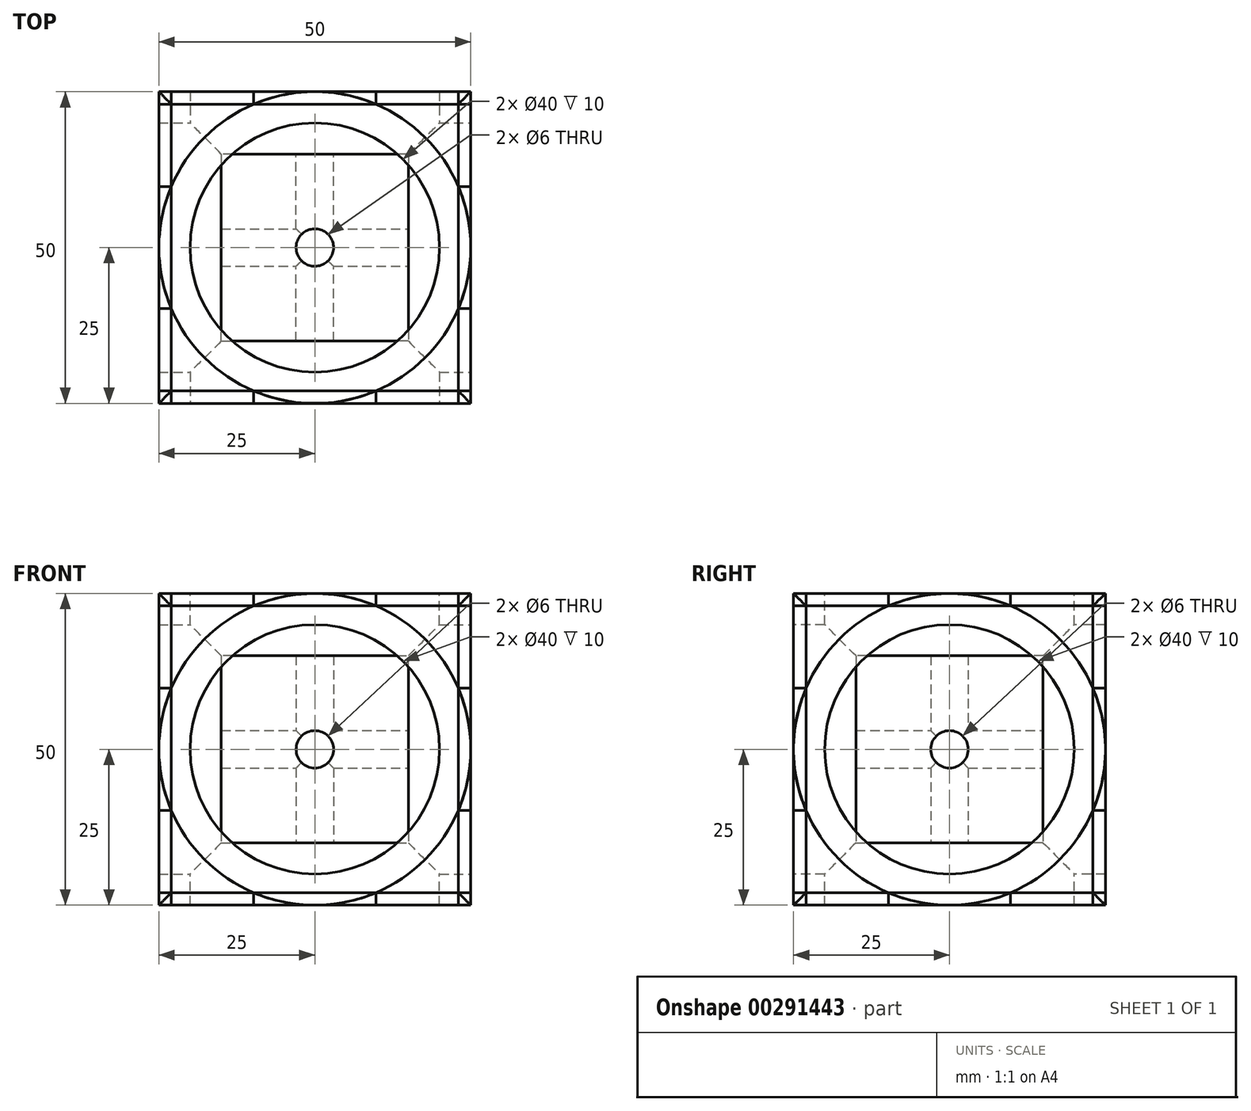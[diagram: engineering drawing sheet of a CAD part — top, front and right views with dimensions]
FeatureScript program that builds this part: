
annotation { "Feature Type Name" : "Feature", "Feature Type Description" : "" }
export const myFeature = defineFeature(function(context is Context, id is Id, definition is map)
    precondition{}
    {
        {
            var Q0;
            Q0=qCreatedBy(makeId("Front.planeOp"),FACE);
            var sketch = newSketch(context, id + "F0", { "sketchPlane" : qUnion([Q0])});
            skLineSegment(sketch, "E0.bottom", {"start": v(-25, 25) * mm, "end": v(25, 25) * mm});
            skLineSegment(sketch, "E0.top", {"start": v(-25, -25) * mm, "end": v(25, -25) * mm});
            skLineSegment(sketch, "E0.left", {"start": v(-25, 25) * mm, "end": v(-25, -25) * mm});
            skLineSegment(sketch, "E0.right", {"start": v(25, 25) * mm, "end": v(25, -25) * mm});
            skSolve(sketch);
        }
        {
            var Q0;
            Q0 = qSketchRegion(id + "F0", true);
            extrude(context, id + "F1", {"entities" : qUnion([Q0]), "depth" : 25 * mm, "hasSecondDirection" : true, "secondDirectionOppositeDirection" : true, "secondDirectionDepth" : 25 * mm});
        }
        {
            var Q0;
            Q0=makeQuery(id+"F1.opExtrude","SWEPT_FACE",FACE,{"disambiguationData":[OSD([sQuery(id+"F0.wireOp",EDGE,"E0.right")])]});
            var sketch = newSketch(context, id + "F2", { "sketchPlane" : qUnion([Q0])});
            skPoint(sketch, "E1", {"position": v(0, 0) * mm});
            skSolve(sketch);
        }
        {
            var Q0;
            Q0=sQuery(id+"F2.wireOp",VERTEX,"E1");
            var Q1;
            Q1=makeQuery(id+"F1.opExtrude","SWEPT_BODY",BODY,{"disambiguationData":[OSD([sQuery(id+"F0.wireOp",EDGE,"E0.bottom"),sQuery(id+"F0.wireOp",EDGE,"E0.top"),sQuery(id+"F0.wireOp",EDGE,"E0.left"),sQuery(id+"F0.wireOp",EDGE,"E0.right")])]});
            hole(context, id + "F3", {"style" : HoleStyle.SIMPLE, "endStyle" : HoleEndStyle.THROUGH, "holeDiameter" : 40 * mm, "tappedDepth" : 12 * mm, "tapClearance" : 3, "locations" : qUnion([Q0]), "scope" : qUnion([Q1])});
        }
        {
            var Q0;
            Q0=makeQuery(id+"F1.opExtrude","SWEPT_FACE",FACE,{"disambiguationData":[OSD([sQuery(id+"F0.wireOp",EDGE,"E0.bottom")])]});
            var sketch = newSketch(context, id + "F4", { "sketchPlane" : qUnion([Q0])});
            skPoint(sketch, "E2", {"position": v(0, 0) * mm});
            skSolve(sketch);
        }
        {
            var Q0;
            Q0=sQuery(id+"F4.wireOp",VERTEX,"E2");
            var Q1;
            Q1=makeQuery(id+"F1.opExtrude","SWEPT_BODY",BODY,{"disambiguationData":[OSD([sQuery(id+"F0.wireOp",EDGE,"E0.bottom"),sQuery(id+"F0.wireOp",EDGE,"E0.top"),sQuery(id+"F0.wireOp",EDGE,"E0.left"),sQuery(id+"F0.wireOp",EDGE,"E0.right")])]});
            hole(context, id + "F5", {"style" : HoleStyle.SIMPLE, "endStyle" : HoleEndStyle.THROUGH, "holeDiameter" : 40 * mm, "tappedDepth" : 12 * mm, "tapClearance" : 3, "locations" : qUnion([Q0]), "scope" : qUnion([Q1])});
        }
        {
            var Q0;
            Q0=makeQuery(id+"F1.opExtrude","CAP_FACE",FACE,{"disambiguationData":[OSD([sQuery(id+"F0.wireOp",EDGE,"E0.bottom"),sQuery(id+"F0.wireOp",EDGE,"E0.top"),sQuery(id+"F0.wireOp",EDGE,"E0.left"),sQuery(id+"F0.wireOp",EDGE,"E0.right")])],"isStart":false});
            var sketch = newSketch(context, id + "F6", { "sketchPlane" : qUnion([Q0])});
            skPoint(sketch, "E3", {"position": v(0, 0) * mm});
            skSolve(sketch);
        }
        {
            var Q0;
            Q0=sQuery(id+"F6.wireOp",VERTEX,"E3");
            var Q1;
            Q1=makeQuery(id+"F1.opExtrude","SWEPT_BODY",BODY,{"disambiguationData":[OSD([sQuery(id+"F0.wireOp",EDGE,"E0.bottom"),sQuery(id+"F0.wireOp",EDGE,"E0.top"),sQuery(id+"F0.wireOp",EDGE,"E0.left"),sQuery(id+"F0.wireOp",EDGE,"E0.right")])]});
            hole(context, id + "F7", {"style" : HoleStyle.SIMPLE, "endStyle" : HoleEndStyle.THROUGH, "holeDiameter" : 40 * mm, "tappedDepth" : 12 * mm, "tapClearance" : 3, "locations" : qUnion([Q0]), "scope" : qUnion([Q1])});
        }
        {
            var Q0;
            Q0=qCreatedBy(makeId("Top.planeOp"),FACE);
            var sketch = newSketch(context, id + "F8", { "sketchPlane" : qUnion([Q0])});
            skLineSegment(sketch, "E4.bottom", {"start": v(-15, 15) * mm, "end": v(15, 15) * mm});
            skLineSegment(sketch, "E4.top", {"start": v(-15, -15) * mm, "end": v(15, -15) * mm});
            skLineSegment(sketch, "E4.left", {"start": v(-15, 15) * mm, "end": v(-15, -15) * mm});
            skLineSegment(sketch, "E4.right", {"start": v(15, 15) * mm, "end": v(15, -15) * mm});
            skSolve(sketch);
        }
        {
            var Q0;
            Q0=makeQuery(id+"F8.imprint","IMPRINT",FACE,{"disambiguationData":[TD([[makeQuery(id+"F8.imprint","IMPRINT",EDGE,{"derivedFrom":sQuery(id+"F8.wireOp",EDGE,"E4.bottom")}),-1.0]])]});
            extrude(context, id + "F9", {"entities" : qUnion([Q0]), "operationType" : NewBodyOperationType.ADD, "depth" : 15 * mm, "hasSecondDirection" : true, "secondDirectionOppositeDirection" : true, "secondDirectionDepth" : 15 * mm});
        }
        {
            var Q0;
            Q0=makeQuery(id+"F1.opExtrude","CAP_FACE",FACE,{"disambiguationData":[OSD([sQuery(id+"F0.wireOp",EDGE,"E0.bottom"),sQuery(id+"F0.wireOp",EDGE,"E0.top"),sQuery(id+"F0.wireOp",EDGE,"E0.left"),sQuery(id+"F0.wireOp",EDGE,"E0.right")])],"isStart":true});
            var sketch = newSketch(context, id + "F10", { "sketchPlane" : qUnion([Q0])});
            skCircle(sketch, "E5", {"center": v(0, 0) * mm, "radius": 25 * mm});
            skLineSegment(sketch, "E6.bottom", {"start": v(25, -25) * mm, "end": v(-25, -25) * mm});
            skLineSegment(sketch, "E6.top", {"start": v(25, 25) * mm, "end": v(-25, 25) * mm});
            skLineSegment(sketch, "E6.left", {"start": v(25, -25) * mm, "end": v(25, 25) * mm});
            skLineSegment(sketch, "E6.right", {"start": v(-25, -25) * mm, "end": v(-25, 25) * mm});
            skSolve(sketch);
        }
        {
            var Q0;
            Q0=makeQuery(id+"F1.opExtrude","SWEPT_FACE",FACE,{"disambiguationData":[OSD([sQuery(id+"F0.wireOp",EDGE,"E0.left")])]});
            var sketch = newSketch(context, id + "F11", { "sketchPlane" : qUnion([Q0])});
            skCircle(sketch, "E7", {"center": v(0, 0) * mm, "radius": 25 * mm});
            skLineSegment(sketch, "E8.bottom", {"start": v(25, -25) * mm, "end": v(-25, -25) * mm});
            skLineSegment(sketch, "E8.top", {"start": v(25, 25) * mm, "end": v(-25, 25) * mm});
            skLineSegment(sketch, "E8.left", {"start": v(25, -25) * mm, "end": v(25, 25) * mm});
            skLineSegment(sketch, "E8.right", {"start": v(-25, -25) * mm, "end": v(-25, 25) * mm});
            skSolve(sketch);
        }
        {
            var Q0;
            Q0=makeQuery(id+"F1.opExtrude","SWEPT_FACE",FACE,{"disambiguationData":[OSD([sQuery(id+"F0.wireOp",EDGE,"E0.bottom")])]});
            var sketch = newSketch(context, id + "F12", { "sketchPlane" : qUnion([Q0])});
            skCircle(sketch, "E9", {"center": v(0, 0) * mm, "radius": 25 * mm});
            skLineSegment(sketch, "E10.bottom", {"start": v(25, -25) * mm, "end": v(-25, -25) * mm});
            skLineSegment(sketch, "E10.top", {"start": v(25, 25) * mm, "end": v(-25, 25) * mm});
            skLineSegment(sketch, "E10.left", {"start": v(25, -25) * mm, "end": v(25, 25) * mm});
            skLineSegment(sketch, "E10.right", {"start": v(-25, -25) * mm, "end": v(-25, 25) * mm});
            skSolve(sketch);
        }
        {
            var Q0;
            Q0=makeQuery(id+"F1.opExtrude","SWEPT_FACE",FACE,{"disambiguationData":[OSD([sQuery(id+"F0.wireOp",EDGE,"E0.right")])]});
            var sketch = newSketch(context, id + "F13", { "sketchPlane" : qUnion([Q0])});
            skCircle(sketch, "E11", {"center": v(0, 0) * mm, "radius": 25 * mm});
            skLineSegment(sketch, "E12.bottom", {"start": v(25, -25) * mm, "end": v(-25, -25) * mm});
            skLineSegment(sketch, "E12.top", {"start": v(25, 25) * mm, "end": v(-25, 25) * mm});
            skLineSegment(sketch, "E12.left", {"start": v(25, -25) * mm, "end": v(25, 25) * mm});
            skLineSegment(sketch, "E12.right", {"start": v(-25, -25) * mm, "end": v(-25, 25) * mm});
            skSolve(sketch);
        }
        {
            var Q0;
            Q0=makeQuery(id+"F1.opExtrude","SWEPT_FACE",FACE,{"disambiguationData":[OSD([sQuery(id+"F0.wireOp",EDGE,"E0.top")])]});
            var sketch = newSketch(context, id + "F14", { "sketchPlane" : qUnion([Q0])});
            skCircle(sketch, "E13", {"center": v(0, 0) * mm, "radius": 25 * mm});
            skLineSegment(sketch, "E14.bottom", {"start": v(25, -25) * mm, "end": v(-25, -25) * mm});
            skLineSegment(sketch, "E14.top", {"start": v(25, 25) * mm, "end": v(-25, 25) * mm});
            skLineSegment(sketch, "E14.left", {"start": v(25, -25) * mm, "end": v(25, 25) * mm});
            skLineSegment(sketch, "E14.right", {"start": v(-25, -25) * mm, "end": v(-25, 25) * mm});
            skSolve(sketch);
        }
        {
            var Q0;
            Q0=makeQuery(id+"F1.opExtrude","CAP_FACE",FACE,{"disambiguationData":[OSD([sQuery(id+"F0.wireOp",EDGE,"E0.bottom"),sQuery(id+"F0.wireOp",EDGE,"E0.top"),sQuery(id+"F0.wireOp",EDGE,"E0.left"),sQuery(id+"F0.wireOp",EDGE,"E0.right")])],"isStart":false});
            var sketch = newSketch(context, id + "F15", { "sketchPlane" : qUnion([Q0])});
            skCircle(sketch, "E15", {"center": v(0, 0) * mm, "radius": 25 * mm});
            skLineSegment(sketch, "E16.bottom", {"start": v(25, -25) * mm, "end": v(-25, -25) * mm});
            skLineSegment(sketch, "E16.top", {"start": v(25, 25) * mm, "end": v(-25, 25) * mm});
            skLineSegment(sketch, "E16.left", {"start": v(25, -25) * mm, "end": v(25, 25) * mm});
            skLineSegment(sketch, "E16.right", {"start": v(-25, -25) * mm, "end": v(-25, 25) * mm});
            skSolve(sketch);
        }
        {
            var Q0;
            Q0=makeQuery(id+"F1.opExtrude","CAP_FACE",FACE,{"disambiguationData":[OSD([sQuery(id+"F0.wireOp",EDGE,"E0.bottom"),sQuery(id+"F0.wireOp",EDGE,"E0.top"),sQuery(id+"F0.wireOp",EDGE,"E0.left"),sQuery(id+"F0.wireOp",EDGE,"E0.right")])],"isStart":true});
            var sketch = newSketch(context, id + "F16", { "sketchPlane" : qUnion([Q0])});
            skCircle(sketch, "E17", {"center": v(0, 0) * mm, "radius": 25 * mm});
            skLineSegment(sketch, "E18.bottom", {"start": v(25, -25) * mm, "end": v(-25, -25) * mm});
            skLineSegment(sketch, "E18.top", {"start": v(25, 25) * mm, "end": v(-25, 25) * mm});
            skLineSegment(sketch, "E18.left", {"start": v(25, -25) * mm, "end": v(25, 25) * mm});
            skLineSegment(sketch, "E18.right", {"start": v(-25, -25) * mm, "end": v(-25, 25) * mm});
            skSolve(sketch);
        }
        {
            var Q0;
            {var subQ0=sQuery(id+"F10.wireOp",EDGE,"E6.top");var subQ1=sQuery(id+"F10.wireOp",EDGE,"E5");var subQ2=makeQuery(id+"F10.imprint","INTERSECT",VERTEX,{"derivedFrom":[subQ1,subQ0]});Q0=makeQuery(id+"F10.imprint","IMPRINT",FACE,{"disambiguationData":[TD([[makeQuery(id+"F10.imprint","IMPRINT",EDGE,{"disambiguationData":[TD([[subQ2,1.0]])],"derivedFrom":subQ1}),-1.0]])]});}
            var Q1;
            {var subQ0=sQuery(id+"F10.wireOp",EDGE,"E6.top");var subQ1=sQuery(id+"F10.wireOp",EDGE,"E5");var subQ2=makeQuery(id+"F10.imprint","INTERSECT",VERTEX,{"derivedFrom":[subQ1,subQ0]});Q1=makeQuery(id+"F10.imprint","IMPRINT",FACE,{"disambiguationData":[TD([[makeQuery(id+"F10.imprint","IMPRINT",EDGE,{"disambiguationData":[TD([[subQ2,-1.0]])],"derivedFrom":subQ1}),-1.0]])]});}
            var Q2;
            {var subQ0=sQuery(id+"F10.wireOp",EDGE,"E6.right");var subQ1=sQuery(id+"F10.wireOp",EDGE,"E5");var subQ2=makeQuery(id+"F10.imprint","INTERSECT",VERTEX,{"derivedFrom":[subQ1,subQ0]});Q2=makeQuery(id+"F10.imprint","IMPRINT",FACE,{"disambiguationData":[TD([[makeQuery(id+"F10.imprint","IMPRINT",EDGE,{"disambiguationData":[TD([[subQ2,-1.0]])],"derivedFrom":subQ1}),-1.0]])]});}
            var Q3;
            {var subQ0=sQuery(id+"F10.wireOp",EDGE,"E6.left");var subQ1=sQuery(id+"F10.wireOp",EDGE,"E5");var subQ2=makeQuery(id+"F10.imprint","INTERSECT",VERTEX,{"derivedFrom":[subQ1,subQ0]});Q3=makeQuery(id+"F10.imprint","IMPRINT",FACE,{"disambiguationData":[TD([[makeQuery(id+"F10.imprint","IMPRINT",EDGE,{"disambiguationData":[TD([[subQ2,1.0]])],"derivedFrom":subQ1}),-1.0]])]});}
            extrude(context, id + "F17", {"entities" : qUnion([Q0, Q1, Q2, Q3]), "operationType" : NewBodyOperationType.REMOVE, "depth" : 2 * mm});
        }
        {
            var Q0;
            {var subQ0=sQuery(id+"F15.wireOp",EDGE,"E16.top");var subQ1=sQuery(id+"F15.wireOp",EDGE,"E15");var subQ2=makeQuery(id+"F15.imprint","INTERSECT",VERTEX,{"derivedFrom":[subQ1,subQ0]});Q0=makeQuery(id+"F15.imprint","IMPRINT",FACE,{"disambiguationData":[TD([[makeQuery(id+"F15.imprint","IMPRINT",EDGE,{"disambiguationData":[TD([[subQ2,-1.0]])],"derivedFrom":subQ1}),-1.0]])]});}
            var Q1;
            {var subQ0=sQuery(id+"F15.wireOp",EDGE,"E16.right");var subQ1=sQuery(id+"F15.wireOp",EDGE,"E15");var subQ2=makeQuery(id+"F15.imprint","INTERSECT",VERTEX,{"derivedFrom":[subQ1,subQ0]});Q1=makeQuery(id+"F15.imprint","IMPRINT",FACE,{"disambiguationData":[TD([[makeQuery(id+"F15.imprint","IMPRINT",EDGE,{"disambiguationData":[TD([[subQ2,-1.0]])],"derivedFrom":subQ1}),-1.0]])]});}
            var Q2;
            {var subQ0=sQuery(id+"F15.wireOp",EDGE,"E16.left");var subQ1=sQuery(id+"F15.wireOp",EDGE,"E15");var subQ2=makeQuery(id+"F15.imprint","INTERSECT",VERTEX,{"derivedFrom":[subQ1,subQ0]});Q2=makeQuery(id+"F15.imprint","IMPRINT",FACE,{"disambiguationData":[TD([[makeQuery(id+"F15.imprint","IMPRINT",EDGE,{"disambiguationData":[TD([[subQ2,1.0]])],"derivedFrom":subQ1}),-1.0]])]});}
            var Q3;
            {var subQ0=sQuery(id+"F15.wireOp",EDGE,"E16.top");var subQ1=sQuery(id+"F15.wireOp",EDGE,"E15");var subQ2=makeQuery(id+"F15.imprint","INTERSECT",VERTEX,{"derivedFrom":[subQ1,subQ0]});Q3=makeQuery(id+"F15.imprint","IMPRINT",FACE,{"disambiguationData":[TD([[makeQuery(id+"F15.imprint","IMPRINT",EDGE,{"disambiguationData":[TD([[subQ2,1.0]])],"derivedFrom":subQ1}),-1.0]])]});}
            extrude(context, id + "F18", {"entities" : qUnion([Q0, Q1, Q2, Q3]), "operationType" : NewBodyOperationType.REMOVE, "oppositeDirection" : true, "depth" : 2 * mm});
        }
        {
            var Q0;
            {var subQ0=sQuery(id+"F12.wireOp",EDGE,"E10.right");var subQ1=sQuery(id+"F12.wireOp",EDGE,"E9");var subQ2=makeQuery(id+"F12.imprint","INTERSECT",VERTEX,{"derivedFrom":[subQ1,subQ0]});Q0=makeQuery(id+"F12.imprint","IMPRINT",FACE,{"disambiguationData":[TD([[makeQuery(id+"F12.imprint","IMPRINT",EDGE,{"disambiguationData":[TD([[subQ2,-1.0]])],"derivedFrom":subQ1}),-1.0]])]});}
            var Q1;
            {var subQ0=sQuery(id+"F12.wireOp",EDGE,"E10.top");var subQ1=sQuery(id+"F12.wireOp",EDGE,"E9");var subQ2=makeQuery(id+"F12.imprint","INTERSECT",VERTEX,{"derivedFrom":[subQ1,subQ0]});Q1=makeQuery(id+"F12.imprint","IMPRINT",FACE,{"disambiguationData":[TD([[makeQuery(id+"F12.imprint","IMPRINT",EDGE,{"disambiguationData":[TD([[subQ2,-1.0]])],"derivedFrom":subQ1}),-1.0]])]});}
            var Q2;
            {var subQ0=sQuery(id+"F12.wireOp",EDGE,"E10.top");var subQ1=sQuery(id+"F12.wireOp",EDGE,"E9");var subQ2=makeQuery(id+"F12.imprint","INTERSECT",VERTEX,{"derivedFrom":[subQ1,subQ0]});Q2=makeQuery(id+"F12.imprint","IMPRINT",FACE,{"disambiguationData":[TD([[makeQuery(id+"F12.imprint","IMPRINT",EDGE,{"disambiguationData":[TD([[subQ2,1.0]])],"derivedFrom":subQ1}),-1.0]])]});}
            var Q3;
            {var subQ0=sQuery(id+"F12.wireOp",EDGE,"E10.left");var subQ1=sQuery(id+"F12.wireOp",EDGE,"E9");var subQ2=makeQuery(id+"F12.imprint","INTERSECT",VERTEX,{"derivedFrom":[subQ1,subQ0]});Q3=makeQuery(id+"F12.imprint","IMPRINT",FACE,{"disambiguationData":[TD([[makeQuery(id+"F12.imprint","IMPRINT",EDGE,{"disambiguationData":[TD([[subQ2,1.0]])],"derivedFrom":subQ1}),-1.0]])]});}
            extrude(context, id + "F19", {"entities" : qUnion([Q0, Q1, Q2, Q3]), "operationType" : NewBodyOperationType.REMOVE, "oppositeDirection" : true, "depth" : 2 * mm});
        }
        {
            var Q0;
            {var subQ0=sQuery(id+"F13.wireOp",EDGE,"E12.top");var subQ1=sQuery(id+"F13.wireOp",EDGE,"E11");var subQ2=makeQuery(id+"F13.imprint","INTERSECT",VERTEX,{"derivedFrom":[subQ1,subQ0]});Q0=makeQuery(id+"F13.imprint","IMPRINT",FACE,{"disambiguationData":[TD([[makeQuery(id+"F13.imprint","IMPRINT",EDGE,{"disambiguationData":[TD([[subQ2,-1.0]])],"derivedFrom":subQ1}),-1.0]])]});}
            var Q1;
            {var subQ0=sQuery(id+"F13.wireOp",EDGE,"E12.top");var subQ1=sQuery(id+"F13.wireOp",EDGE,"E11");var subQ2=makeQuery(id+"F13.imprint","INTERSECT",VERTEX,{"derivedFrom":[subQ1,subQ0]});Q1=makeQuery(id+"F13.imprint","IMPRINT",FACE,{"disambiguationData":[TD([[makeQuery(id+"F13.imprint","IMPRINT",EDGE,{"disambiguationData":[TD([[subQ2,1.0]])],"derivedFrom":subQ1}),-1.0]])]});}
            var Q2;
            {var subQ0=sQuery(id+"F13.wireOp",EDGE,"E12.left");var subQ1=sQuery(id+"F13.wireOp",EDGE,"E11");var subQ2=makeQuery(id+"F13.imprint","INTERSECT",VERTEX,{"derivedFrom":[subQ1,subQ0]});Q2=makeQuery(id+"F13.imprint","IMPRINT",FACE,{"disambiguationData":[TD([[makeQuery(id+"F13.imprint","IMPRINT",EDGE,{"disambiguationData":[TD([[subQ2,1.0]])],"derivedFrom":subQ1}),-1.0]])]});}
            var Q3;
            {var subQ0=sQuery(id+"F13.wireOp",EDGE,"E12.right");var subQ1=sQuery(id+"F13.wireOp",EDGE,"E11");var subQ2=makeQuery(id+"F13.imprint","INTERSECT",VERTEX,{"derivedFrom":[subQ1,subQ0]});Q3=makeQuery(id+"F13.imprint","IMPRINT",FACE,{"disambiguationData":[TD([[makeQuery(id+"F13.imprint","IMPRINT",EDGE,{"disambiguationData":[TD([[subQ2,-1.0]])],"derivedFrom":subQ1}),-1.0]])]});}
            extrude(context, id + "F20", {"entities" : qUnion([Q0, Q1, Q2, Q3]), "operationType" : NewBodyOperationType.REMOVE, "oppositeDirection" : true, "depth" : 2 * mm});
        }
        {
            var Q0;
            {var subQ0=sQuery(id+"F16.wireOp",EDGE,"E18.top");var subQ1=sQuery(id+"F16.wireOp",EDGE,"E17");var subQ2=makeQuery(id+"F16.imprint","INTERSECT",VERTEX,{"derivedFrom":[subQ1,subQ0]});Q0=makeQuery(id+"F16.imprint","IMPRINT",FACE,{"disambiguationData":[TD([[makeQuery(id+"F16.imprint","IMPRINT",EDGE,{"disambiguationData":[TD([[subQ2,-1.0]])],"derivedFrom":subQ1}),-1.0]])]});}
            var Q1;
            {var subQ0=sQuery(id+"F16.wireOp",EDGE,"E18.top");var subQ1=sQuery(id+"F16.wireOp",EDGE,"E17");var subQ2=makeQuery(id+"F16.imprint","INTERSECT",VERTEX,{"derivedFrom":[subQ1,subQ0]});Q1=makeQuery(id+"F16.imprint","IMPRINT",FACE,{"disambiguationData":[TD([[makeQuery(id+"F16.imprint","IMPRINT",EDGE,{"disambiguationData":[TD([[subQ2,1.0]])],"derivedFrom":subQ1}),-1.0]])]});}
            var Q2;
            {var subQ0=sQuery(id+"F16.wireOp",EDGE,"E18.left");var subQ1=sQuery(id+"F16.wireOp",EDGE,"E17");var subQ2=makeQuery(id+"F16.imprint","INTERSECT",VERTEX,{"derivedFrom":[subQ1,subQ0]});Q2=makeQuery(id+"F16.imprint","IMPRINT",FACE,{"disambiguationData":[TD([[makeQuery(id+"F16.imprint","IMPRINT",EDGE,{"disambiguationData":[TD([[subQ2,1.0]])],"derivedFrom":subQ1}),-1.0]])]});}
            var Q3;
            {var subQ0=sQuery(id+"F16.wireOp",EDGE,"E18.right");var subQ1=sQuery(id+"F16.wireOp",EDGE,"E17");var subQ2=makeQuery(id+"F16.imprint","INTERSECT",VERTEX,{"derivedFrom":[subQ1,subQ0]});Q3=makeQuery(id+"F16.imprint","IMPRINT",FACE,{"disambiguationData":[TD([[makeQuery(id+"F16.imprint","IMPRINT",EDGE,{"disambiguationData":[TD([[subQ2,-1.0]])],"derivedFrom":subQ1}),-1.0]])]});}
            extrude(context, id + "F21", {"entities" : qUnion([Q0, Q1, Q2, Q3]), "operationType" : NewBodyOperationType.REMOVE, "oppositeDirection" : true, "depth" : 2 * mm});
        }
        {
            var Q0;
            {var subQ0=sQuery(id+"F11.wireOp",EDGE,"E8.top");var subQ1=sQuery(id+"F11.wireOp",EDGE,"E7");var subQ2=makeQuery(id+"F11.imprint","INTERSECT",VERTEX,{"derivedFrom":[subQ1,subQ0]});Q0=makeQuery(id+"F11.imprint","IMPRINT",FACE,{"disambiguationData":[TD([[makeQuery(id+"F11.imprint","IMPRINT",EDGE,{"disambiguationData":[TD([[subQ2,-1.0]])],"derivedFrom":subQ1}),-1.0]])]});}
            var Q1;
            {var subQ0=sQuery(id+"F11.wireOp",EDGE,"E8.top");var subQ1=sQuery(id+"F11.wireOp",EDGE,"E7");var subQ2=makeQuery(id+"F11.imprint","INTERSECT",VERTEX,{"derivedFrom":[subQ1,subQ0]});Q1=makeQuery(id+"F11.imprint","IMPRINT",FACE,{"disambiguationData":[TD([[makeQuery(id+"F11.imprint","IMPRINT",EDGE,{"disambiguationData":[TD([[subQ2,1.0]])],"derivedFrom":subQ1}),-1.0]])]});}
            var Q2;
            {var subQ0=sQuery(id+"F11.wireOp",EDGE,"E8.left");var subQ1=sQuery(id+"F11.wireOp",EDGE,"E7");var subQ2=makeQuery(id+"F11.imprint","INTERSECT",VERTEX,{"derivedFrom":[subQ1,subQ0]});Q2=makeQuery(id+"F11.imprint","IMPRINT",FACE,{"disambiguationData":[TD([[makeQuery(id+"F11.imprint","IMPRINT",EDGE,{"disambiguationData":[TD([[subQ2,1.0]])],"derivedFrom":subQ1}),-1.0]])]});}
            var Q3;
            {var subQ0=sQuery(id+"F11.wireOp",EDGE,"E8.right");var subQ1=sQuery(id+"F11.wireOp",EDGE,"E7");var subQ2=makeQuery(id+"F11.imprint","INTERSECT",VERTEX,{"derivedFrom":[subQ1,subQ0]});Q3=makeQuery(id+"F11.imprint","IMPRINT",FACE,{"disambiguationData":[TD([[makeQuery(id+"F11.imprint","IMPRINT",EDGE,{"disambiguationData":[TD([[subQ2,-1.0]])],"derivedFrom":subQ1}),-1.0]])]});}
            extrude(context, id + "F22", {"entities" : qUnion([Q0, Q1, Q2, Q3]), "operationType" : NewBodyOperationType.REMOVE, "oppositeDirection" : true, "depth" : 2 * mm});
        }
        {
            var Q0;
            {var subQ0=sQuery(id+"F14.wireOp",EDGE,"E14.top");var subQ1=sQuery(id+"F14.wireOp",EDGE,"E13");var subQ2=makeQuery(id+"F14.imprint","INTERSECT",VERTEX,{"derivedFrom":[subQ1,subQ0]});Q0=makeQuery(id+"F14.imprint","IMPRINT",FACE,{"disambiguationData":[TD([[makeQuery(id+"F14.imprint","IMPRINT",EDGE,{"disambiguationData":[TD([[subQ2,-1.0]])],"derivedFrom":subQ1}),-1.0]])]});}
            var Q1;
            {var subQ0=sQuery(id+"F14.wireOp",EDGE,"E14.right");var subQ1=sQuery(id+"F14.wireOp",EDGE,"E13");var subQ2=makeQuery(id+"F14.imprint","INTERSECT",VERTEX,{"derivedFrom":[subQ1,subQ0]});Q1=makeQuery(id+"F14.imprint","IMPRINT",FACE,{"disambiguationData":[TD([[makeQuery(id+"F14.imprint","IMPRINT",EDGE,{"disambiguationData":[TD([[subQ2,-1.0]])],"derivedFrom":subQ1}),-1.0]])]});}
            var Q2;
            {var subQ0=sQuery(id+"F14.wireOp",EDGE,"E14.left");var subQ1=sQuery(id+"F14.wireOp",EDGE,"E13");var subQ2=makeQuery(id+"F14.imprint","INTERSECT",VERTEX,{"derivedFrom":[subQ1,subQ0]});Q2=makeQuery(id+"F14.imprint","IMPRINT",FACE,{"disambiguationData":[TD([[makeQuery(id+"F14.imprint","IMPRINT",EDGE,{"disambiguationData":[TD([[subQ2,1.0]])],"derivedFrom":subQ1}),-1.0]])]});}
            var Q3;
            {var subQ0=sQuery(id+"F14.wireOp",EDGE,"E14.top");var subQ1=sQuery(id+"F14.wireOp",EDGE,"E13");var subQ2=makeQuery(id+"F14.imprint","INTERSECT",VERTEX,{"derivedFrom":[subQ1,subQ0]});Q3=makeQuery(id+"F14.imprint","IMPRINT",FACE,{"disambiguationData":[TD([[makeQuery(id+"F14.imprint","IMPRINT",EDGE,{"disambiguationData":[TD([[subQ2,1.0]])],"derivedFrom":subQ1}),-1.0]])]});}
            extrude(context, id + "F23", {"entities" : qUnion([Q0, Q1, Q2, Q3]), "operationType" : NewBodyOperationType.REMOVE, "oppositeDirection" : true, "depth" : 2 * mm});
        }
        {
            var Q0;
            Q0=makeQuery(id+"F9.opExtrude","SWEPT_FACE",FACE,{"disambiguationData":[OSD([sQuery(id+"F8.wireOp",EDGE,"E4.right")])]});
            var sketch = newSketch(context, id + "F24", { "sketchPlane" : qUnion([Q0])});
            skPoint(sketch, "E19", {"position": v(0, 0) * mm});
            skSolve(sketch);
        }
        {
            var Q0;
            Q0=sQuery(id+"F24.wireOp",VERTEX,"E19");
            var Q1;
            Q1=makeQuery(id+"F1.opExtrude","SWEPT_BODY",BODY,{"disambiguationData":[OSD([sQuery(id+"F0.wireOp",EDGE,"E0.bottom"),sQuery(id+"F0.wireOp",EDGE,"E0.top"),sQuery(id+"F0.wireOp",EDGE,"E0.left"),sQuery(id+"F0.wireOp",EDGE,"E0.right")])]});
            hole(context, id + "F25", {"style" : HoleStyle.SIMPLE, "endStyle" : HoleEndStyle.THROUGH, "holeDiameter" : 6 * mm, "tappedDepth" : 12 * mm, "tapClearance" : 3, "locations" : qUnion([Q0]), "scope" : qUnion([Q1])});
        }
        {
            var Q0;
            Q0=makeQuery(id+"F9.opExtrude","SWEPT_FACE",FACE,{"disambiguationData":[OSD([sQuery(id+"F8.wireOp",EDGE,"E4.bottom")])]});
            var sketch = newSketch(context, id + "F26", { "sketchPlane" : qUnion([Q0])});
            skPoint(sketch, "E20", {"position": v(0, 0) * mm});
            skSolve(sketch);
        }
        {
            var Q0;
            Q0=sQuery(id+"F26.wireOp",VERTEX,"E20");
            var Q1;
            Q1=makeQuery(id+"F1.opExtrude","SWEPT_BODY",BODY,{"disambiguationData":[OSD([sQuery(id+"F0.wireOp",EDGE,"E0.bottom"),sQuery(id+"F0.wireOp",EDGE,"E0.top"),sQuery(id+"F0.wireOp",EDGE,"E0.left"),sQuery(id+"F0.wireOp",EDGE,"E0.right")])]});
            hole(context, id + "F27", {"style" : HoleStyle.SIMPLE, "endStyle" : HoleEndStyle.THROUGH, "holeDiameter" : 6 * mm, "tappedDepth" : 12 * mm, "tapClearance" : 3, "locations" : qUnion([Q0]), "scope" : qUnion([Q1])});
        }
        {
            var Q0;
            Q0=makeQuery(id+"F9.opExtrude","CAP_FACE",FACE,{"disambiguationData":[OSD([sQuery(id+"F8.wireOp",EDGE,"E4.bottom"),sQuery(id+"F8.wireOp",EDGE,"E4.top"),sQuery(id+"F8.wireOp",EDGE,"E4.left"),sQuery(id+"F8.wireOp",EDGE,"E4.right")])],"isStart":true});
            var sketch = newSketch(context, id + "F28", { "sketchPlane" : qUnion([Q0])});
            skPoint(sketch, "E21", {"position": v(0, 0) * mm});
            skSolve(sketch);
        }
        {
            var Q0;
            Q0=sQuery(id+"F28.wireOp",VERTEX,"E21");
            var Q1;
            Q1=makeQuery(id+"F1.opExtrude","SWEPT_BODY",BODY,{"disambiguationData":[OSD([sQuery(id+"F0.wireOp",EDGE,"E0.bottom"),sQuery(id+"F0.wireOp",EDGE,"E0.top"),sQuery(id+"F0.wireOp",EDGE,"E0.left"),sQuery(id+"F0.wireOp",EDGE,"E0.right")])]});
            hole(context, id + "F29", {"style" : HoleStyle.SIMPLE, "endStyle" : HoleEndStyle.THROUGH, "holeDiameter" : 6 * mm, "tappedDepth" : 12 * mm, "tapClearance" : 3, "locations" : qUnion([Q0]), "scope" : qUnion([Q1])});
        }
    });
